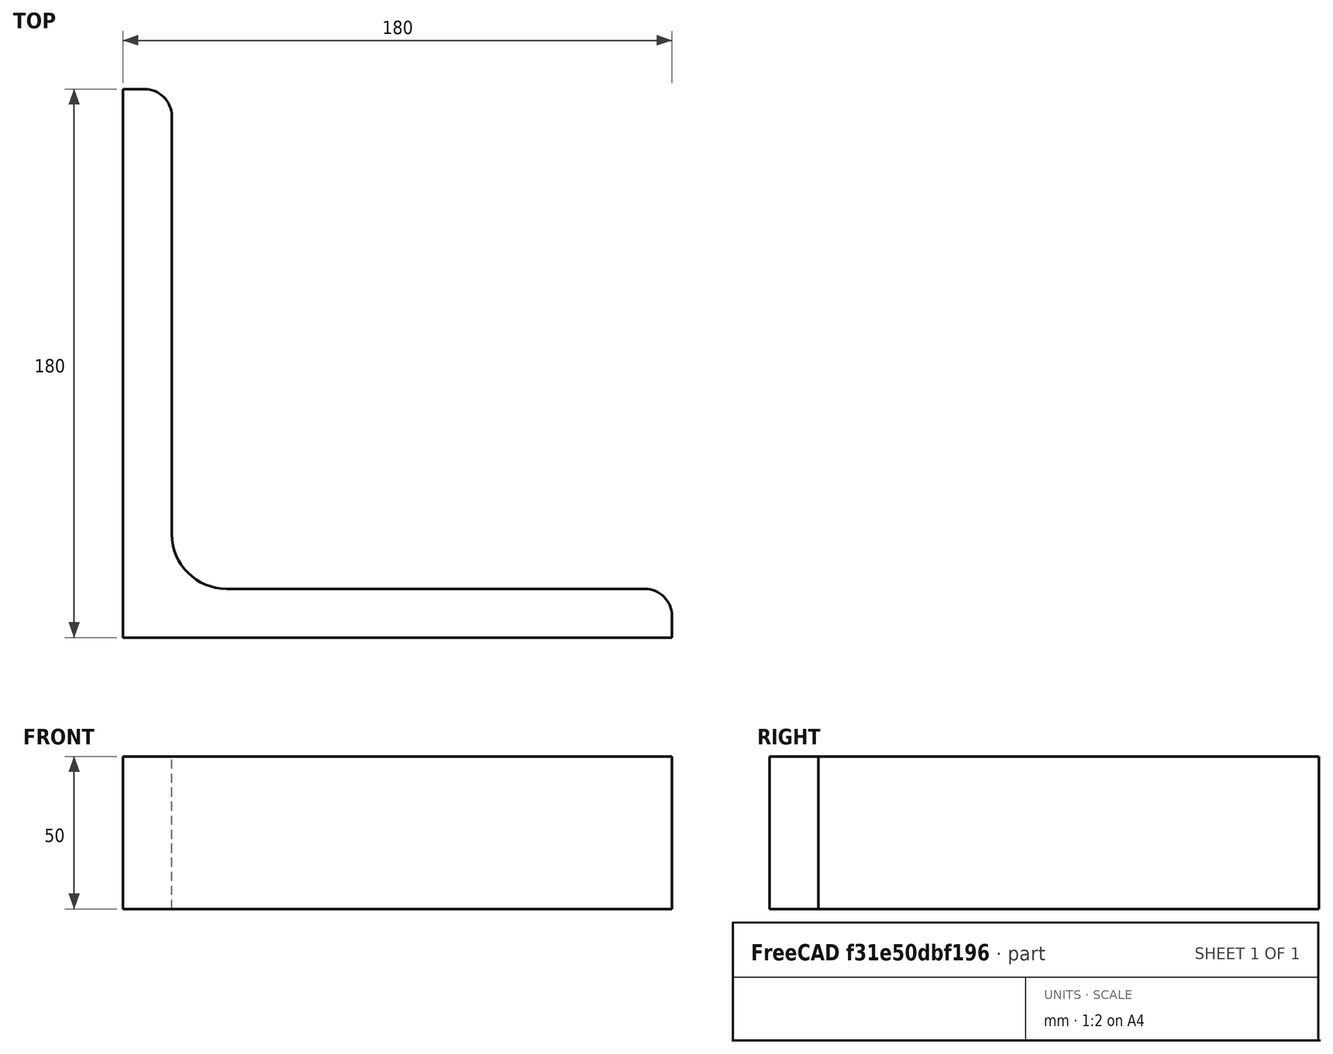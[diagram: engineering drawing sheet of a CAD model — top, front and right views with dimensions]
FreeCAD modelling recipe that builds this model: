
FCSTD DOCUMENT  (FreeCAD 0.15R4671 (Git))
Label: Angle Bar L180x180x16 EN10056 S235JR
License: All rights reserved
LicenseURL: http://en.wikipedia.org/wiki/All_rights_reserved
objects: Sketcher::SketchObject×1, Part::Extrusion×1
note: 2 computed .brp shape members not serialized (recipe doc carries the construction recipe); baked Part::Feature solids carry a one-line shape summary decoded from their .brp

FEATURE [Sketcher::SketchObject] Sketch
  sketch-geometry (9):
    g0: LineSegment StartX=0 StartY=0 StartZ=0 EndX=180 EndY=0 EndZ=0
    g1: LineSegment StartX=180 StartY=0 StartZ=0 EndX=180 EndY=7 EndZ=0
    g2: LineSegment StartX=171 StartY=16 StartZ=0 EndX=34 EndY=16 EndZ=0
    g3: LineSegment StartX=0 StartY=0 StartZ=0 EndX=0 EndY=180 EndZ=0
    g4: LineSegment StartX=0 StartY=180 StartZ=0 EndX=7 EndY=180 EndZ=0
    g5: LineSegment StartX=16 StartY=171 StartZ=0 EndX=16 EndY=34 EndZ=0
    g6: ArcOfCircle CenterX=34 CenterY=34 CenterZ=0 NormalX=0 NormalY=0 NormalZ=1 Radius=18 StartAngle=3.14159 EndAngle=4.71239
    g7: ArcOfCircle CenterX=7 CenterY=171 CenterZ=0 NormalX=0 NormalY=0 NormalZ=1 Radius=9 StartAngle=0 EndAngle=1.5708
    g8: ArcOfCircle CenterX=171 CenterY=7 CenterZ=0 NormalX=0 NormalY=0 NormalZ=1 Radius=9 StartAngle=0 EndAngle=1.5708
  constraints (23):
    c: Coincident(g0,g-1)
    c: Horizontal(g0)
    c: Coincident(g1,g0)
    c: Vertical(g1)
    c: Horizontal(g2)
    c: Coincident(g3,g-1)
    c: Vertical(g3)
    c: Coincident(g4,g3)
    c: Horizontal(g4)
    c: Vertical(g5)
    c: Tangent(g5,g6) = -1.5708
    c: Tangent(g2,g6) = 1.5708
    c: Tangent(g4,g7) = 1.5708
    c: Tangent(g5,g7) = 1.5708
    c: Tangent(g2,g8) = -1.5708
    c: Tangent(g1,g8) = -1.5708
    c: DistanceX(g0) = 180
    c: DistanceY(g3) = 180
    c: DistanceY(g0,g2) = 16
    c: DistanceX(g3,g5) = 16
    c: Radius(g6) = 18
    c: Radius(g8) = 9
    c: Radius(g7) = 9
FEATURE [Part::Extrusion] Extrude  label="Angle Bar L180x180x16 EN10056 S235JR"
  Base = -> Sketch
  Dir = (0,0,50)
  Solid = true
